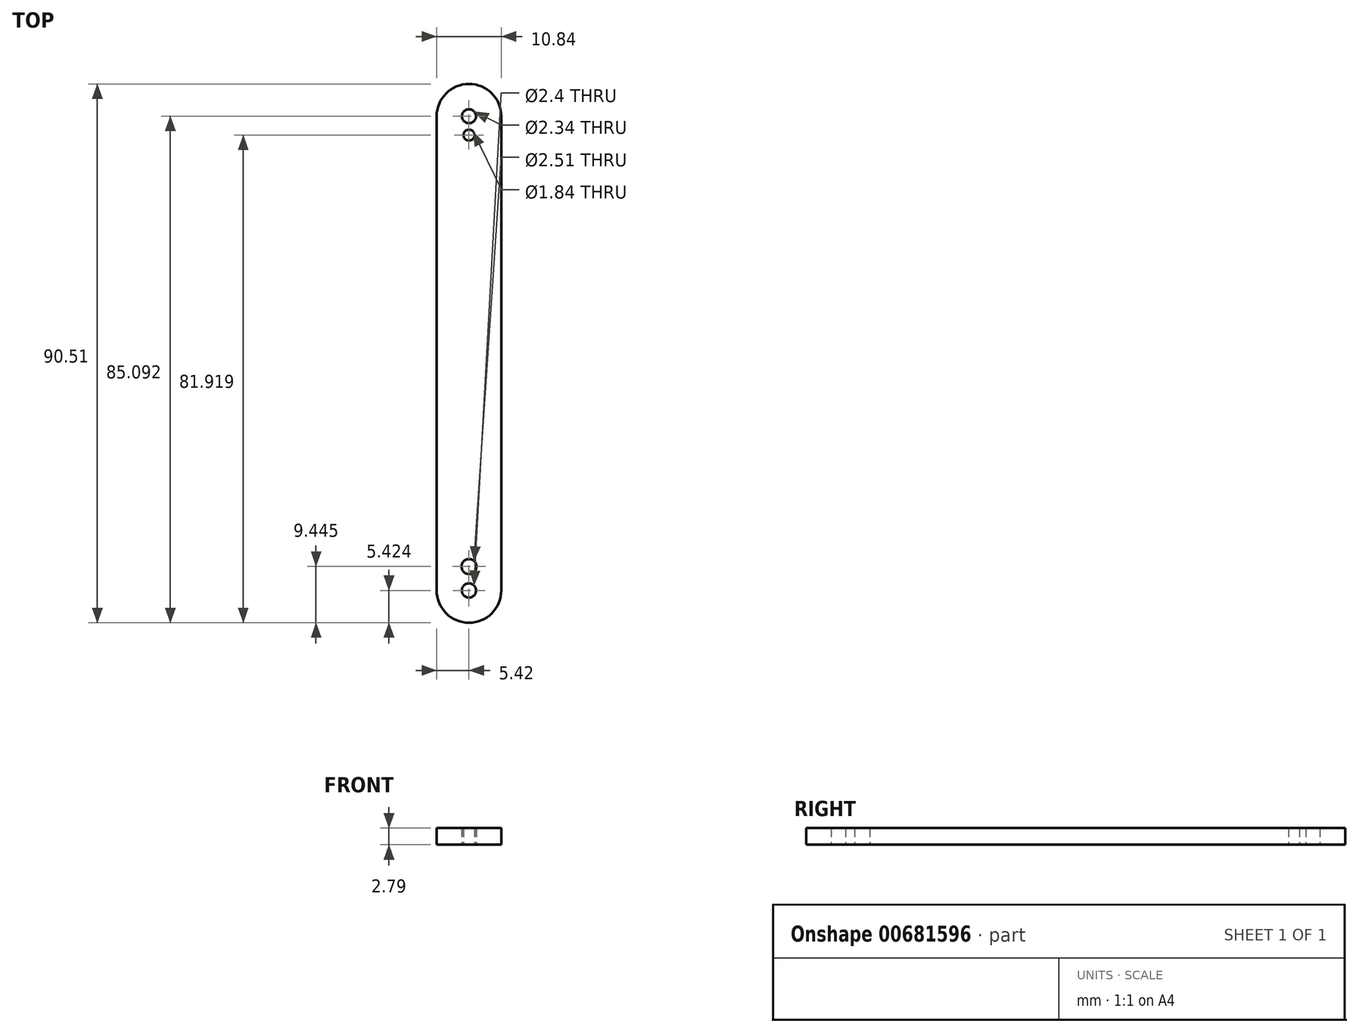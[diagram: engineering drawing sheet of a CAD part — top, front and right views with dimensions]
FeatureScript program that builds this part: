
annotation { "Feature Type Name" : "Feature", "Feature Type Description" : "" }
export const myFeature = defineFeature(function(context is Context, id is Id, definition is map)
    precondition{}
    {
        {
            var Q0;
            Q0=qCreatedBy(makeId("Top.planeOp"),FACE);
            var sketch = newSketch(context, id + "F0", { "sketchPlane" : qUnion([Q0])});
            skLineSegment(sketch, "E0.left", {"start": v(5.42, 40.64) * mm, "end": v(5.42, -39.03) * mm});
            skLineSegment(sketch, "E0.right", {"start": v(-5.42, 40.64) * mm, "end": v(-5.42, -39.03) * mm});
            skPoint(sketch, "E0.middle", {"position": v(0, 0.8) * mm});
            skArc(sketch, "E1", {"start": v(-5.42, -39.03) * mm, "mid": v(0, -44.45) * mm, "end": v(5.42, -39.03) * mm});
            skArc(sketch, "E2", {"start": v(5.42, 40.64) * mm, "mid": v(0, 46.06) * mm, "end": v(-5.42, 40.64) * mm});
            skCircle(sketch, "E3", {"center": v(0, -39.03) * mm, "radius": 1.2 * mm});
            skCircle(sketch, "E4", {"center": v(0, 40.64) * mm, "radius": 1.17 * mm});
            skCircle(sketch, "E5", {"center": v(0, -35) * mm, "radius": 1.26 * mm});
            skCircle(sketch, "E6", {"center": v(0, 37.47) * mm, "radius": 0.92 * mm});
            skSolve(sketch);
        }
        {
            var Q0;
            Q0=qSketchRegion(id+"F0",true);
            extrude(context, id + "F1", {"entities" : qUnion([Q0]), "depth" : 2.8 * mm, "offsetDistance" : 25.4 * mm});
        }
    });
